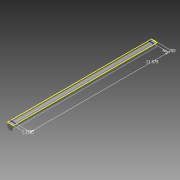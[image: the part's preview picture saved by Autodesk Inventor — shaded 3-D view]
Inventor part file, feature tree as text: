
AUTODESK INVENTOR PART (.ipt)
format: ipt  version: 2012 (Build 160160000, 160)  size: 91,136 bytes
history: native  units: in
note: dims shown in document units (in); Inventor stores cm internally (conversion verified against a paired STEP export)
features: sketch x4, extrude x3, plane x3, projected_geometry x1
ambient origin geometry x8: Origin, YZ Plane, XZ Plane, XY Plane, X Axis, Y Axis, Z Axis, Center Point
bodies: Solid1 (feature_tree)
feature tree (11):
  extrude  "Extrusion1"  Depth=12.375in TaperAngle=0.0deg
  plane  "Work Plane1"
  sketch  "Sketch2"  dims[d3=11.875in d4=0.25in]
  plane  "Work Plane2"
  plane  "Work Plane3"
  extrude  "Extrusion2"  Depth=0.25in
  extrude  "Extrusion3"  Depth=0.4in
  sketch  "Sketch1"  dims[d0=0.5in d1=12.375in d2=0.0in]
  projected_geometry  "Projected Loop1"
  sketch  "Sketch3"  dims[d5=0.25in d6=0.4in]
  sketch  "Sketch4"  dims[d7=0.04in d8=0.0in d9=0.04in d10=0.0in]
